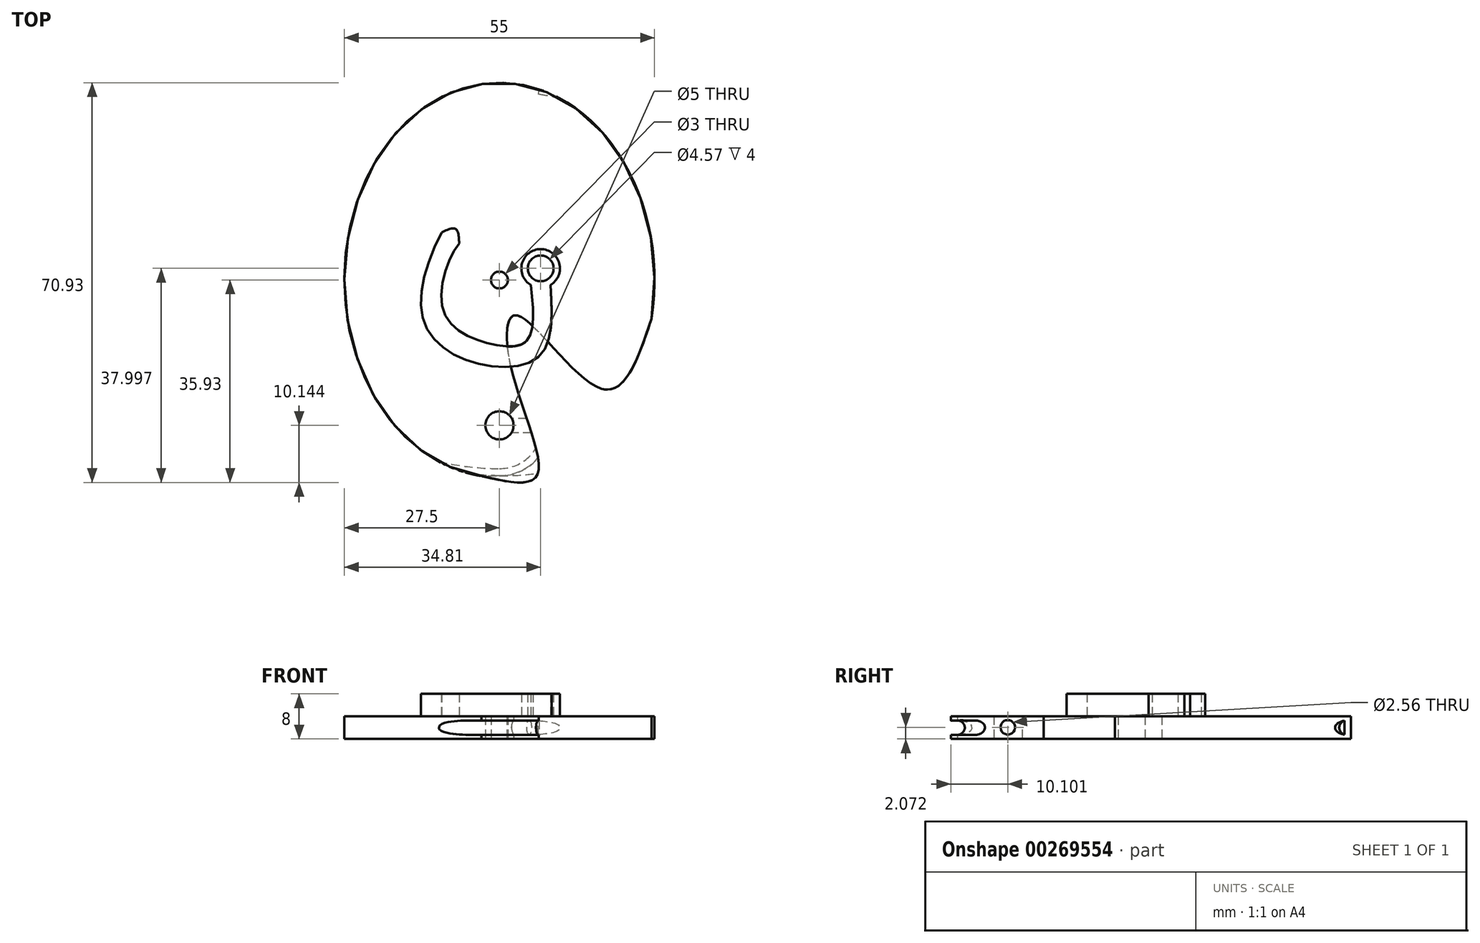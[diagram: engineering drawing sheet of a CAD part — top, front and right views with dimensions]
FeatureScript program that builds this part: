
annotation { "Feature Type Name" : "Feature", "Feature Type Description" : "" }
export const myFeature = defineFeature(function(context is Context, id is Id, definition is map)
    precondition{}
    {
        {
            var Q0;
            Q0=qCreatedBy(makeId("Top.planeOp"),FACE);
            var sketch = newSketch(context, id + "F2", { "sketchPlane" : qUnion([Q0])});
            skCircle(sketch, "E0", {"center": v(0, -25.79) * mm, "radius": 2.5 * mm});
            skEllipticalArc(sketch, "E1.trimOffspring", {});
            skPoint(sketch, "E2.3.internal.orphan", {"position": v(9.5, 0) * mm});
            skPoint(sketch, "E3.0.internal.orphan", {"position": v(18.35, -6.83) * mm});
            skPoint(sketch, "E3.1.internal.orphan", {"position": v(23.13, -20.33) * mm});
            skPoint(sketch, "E3.2.internal.orphan", {"position": v(26.97, -6.83) * mm});
            skPoint(sketch, "E4.orphan", {"position": v(23.13, -14.08) * mm});
            skFitSpline(sketch, "E5", {"points": [v(-3.19, -34.76) * mm, v(6.6, -34.76) * mm, v(2.01, -15.29) * mm, v(3.15, -6.29) * mm, v(18.34, -19.35) * mm, v(26.97, -6.83) * mm], "startDerivative": vector(78.13, -18.35) * mm, "endDerivative": vector(32.68, 98.5) * mm});
            skCircle(sketch, "E6", {"center": v(0, 0) * mm, "radius": 1.5 * mm});
            const initialGuessFD7VVaR5RRnER9FFF_0  = {"E1.trimOffspring": [0, 0, 0, -1, 0.035, 0.0275, 1.3742742962770849, 6.167059260959714]};
            skSetInitialGuess(sketch, initialGuessFD7VVaR5RRnER9FFF_0);
            skSolve(sketch);
        }
        {
            var Q0;
            Q0=makeQuery(id+"F2.imprint","IMPRINT",FACE,{"disambiguationData":[TD([[makeQuery(id+"F2.imprint","IMPRINT",EDGE,{"derivedFrom":sQuery(id+"F2.wireOp",EDGE,"E0")}),-1.0]])]});
            extrude(context, id + "F3", {"entities" : qUnion([Q0]), "depth" : 4 * mm});
        }
        {
            var Q0;
            Q0=qCreatedBy(makeId("Right.planeOp"),FACE);
            var sketch = newSketch(context, id + "F4", { "sketchPlane" : qUnion([Q0])});
            skCircle(sketch, "E7", {"center": v(-25.83, 2.07) * mm, "radius": 1.28 * mm});
            skSolve(sketch);
        }
        {
            var Q0;
            Q0=qSketchRegion(id+"F4",true);
            extrude(context, id + "F0", {"entities" : qUnion([Q0]), "operationType" : NewBodyOperationType.REMOVE, "depth" : 25 * mm});
        }
        {
            var Q0;
            Q0=qCreatedBy(makeId("Right.planeOp"),FACE);
            var sketch = newSketch(context, id + "F5", { "sketchPlane" : qUnion([Q0])});
            skArc(sketch, "E8", {"start": v(-34.7, 0.74) * mm, "mid": v(-33.46, 2.04) * mm, "end": v(-34.76, 3.29) * mm});
            skLineSegment(sketch, "E9", {"start": v(-34.76, 3.29) * mm, "end": v(-34.7, 0.74) * mm});
            skLineSegment(sketch, "E10", {"start": v(-34.7, 0.74) * mm, "end": v(-38.27, 0.74) * mm});
            skLineSegment(sketch, "E11", {"start": v(-38.27, 0.74) * mm, "end": v(-38.27, 3.3) * mm});
            skLineSegment(sketch, "E12", {"start": v(-38.27, 3.3) * mm, "end": v(-34.76, 3.29) * mm});
            skSolve(sketch);
        }
        {
            var Q0;
            Q0=qSketchRegion(id+"F5",true);
            var Q1;
            Q1=makeQuery(id+"F3.opExtrude","CAP_EDGE",EDGE,{"disambiguationData":[OSD([sQuery(id+"F2.wireOp",EDGE,"E1.trimOffspring")])],"isStart":false});
            sweep(context, id + "F6", {"operationType" : NewBodyOperationType.REMOVE, "profiles" : qUnion([Q0]), "path" : qUnion([Q1])});
        }
        {
            var Q0;
            Q0=qSketchRegion(id+"F5",true);
            var Q1;
            Q1=makeQuery(id+"F3.opExtrude","CAP_EDGE",EDGE,{"disambiguationData":[OSD([sQuery(id+"F2.wireOp",EDGE,"E0")])],"isStart":false});
            revolve(context, id + "F7", {"operationType" : NewBodyOperationType.REMOVE, "entities" : qUnion([Q0]), "axis" : qUnion([Q1]), "revolveType" : RevolveType.ONE_DIRECTION, "angle" : 90 * degree});
        }
        {
            var Q0;
            Q0=makeQuery(id+"F3.opExtrude","CAP_FACE",FACE,{"disambiguationData":[OSD([sQuery(id+"F2.wireOp",EDGE,"E0"),sQuery(id+"F2.wireOp",EDGE,"E1.trimOffspring"),sQuery(id+"F2.wireOp",EDGE,"E5"),sQuery(id+"F2.wireOp",EDGE,"E6")])],"isStart":false});
            var sketch = newSketch(context, id + "F8", { "sketchPlane" : qUnion([Q0])});
            skArc(sketch, "E13", {"start": v(9.06, -0.87) * mm, "mid": v(7.31, 5.49) * mm, "end": v(5.56, -0.87) * mm});
            skFitSpline(sketch, "E14", {"points": [v(9.06, -0.87) * mm, v(7.35, -13.2) * mm, v(-3.66, -14.86) * mm, v(-13.27, -7.67) * mm, v(-10.23, 8.47) * mm], "startDerivative": vector(3.16, -59.25) * mm, "endDerivative": vector(31.46, 59.29) * mm});
            skFitSpline(sketch, "E15", {"points": [v(5.56, -0.87) * mm, v(4.95, -10.66) * mm, v(-1.28, -11.39) * mm, v(-9.91, -5.54) * mm, v(-7.15, 6.5) * mm, v(-3.66, 8.47) * mm], "startDerivative": vector(5.88, -55.7) * mm, "endDerivative": vector(26.85, 5.5) * mm});
            skFitSpline(sketch, "E16", {"points": [v(-7.15, 6.5) * mm, v(-7.76, 9.05) * mm, v(-10.23, 8.47) * mm], "startDerivative": vector(-0.28, 6.63) * mm, "endDerivative": vector(-5.9, -2.73) * mm});
            skCircle(sketch, "E17", {"center": v(7.31, 2.07) * mm, "radius": 2.29 * mm});
            skPoint(sketch, "E18", {"position": v(0, 0) * mm});
            skSolve(sketch);
        }
        {
            var Q0;
            {var subQ1=sQuery(id+"F8.wireOp",EDGE,"E13");Q0=makeQuery(id+"F8.imprint","IMPRINT",FACE,{"disambiguationData":[TD([[makeQuery(id+"F8.imprint","IMPRINT",EDGE,{"derivedFrom":subQ1}),1.0]])]});}
            var Q1;
            {var subQ0=sQuery(id+"F8.wireOp",EDGE,"E14");var subQ1=makeQuery(id+"F3.opExtrude","CAP_EDGE",EDGE,{"disambiguationData":[OSD([sQuery(id+"F2.wireOp",EDGE,"E5")])],"isStart":false});var subQ2=makeQuery(id+"F8.imprint","INTERSECT",VERTEX,{"disambiguationData":[OD(0.0)],"derivedFrom":[subQ1,subQ0]});Q1=makeQuery(id+"F8.imprint","IMPRINT",FACE,{"disambiguationData":[TD([[makeQuery(id+"F8.imprint","IMPRINT",EDGE,{"disambiguationData":[TD([[subQ2,-1.0]])],"derivedFrom":subQ0}),-1.0]])]});}
            var Q2;
            {var subQ0=sQuery(id+"F8.wireOp",EDGE,"E16");Q2=makeQuery(id+"F8.imprint","IMPRINT",FACE,{"disambiguationData":[TD([[makeQuery(id+"F8.imprint","IMPRINT",EDGE,{"derivedFrom":subQ0}),1.0]])]});}
            extrude(context, id + "F1", {"entities" : qUnion([Q0, Q1, Q2]), "operationType" : NewBodyOperationType.ADD, "depth" : 4 * mm});
        }
    });
